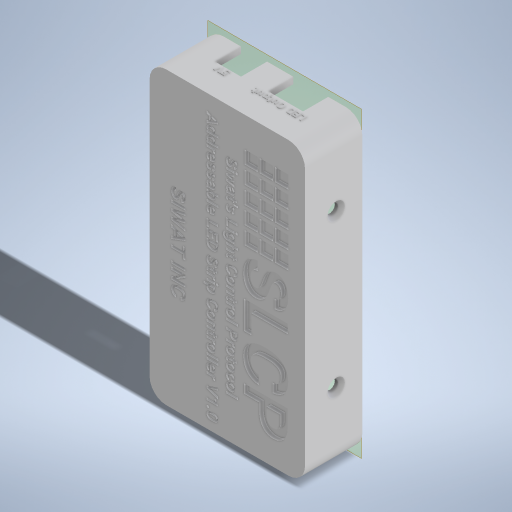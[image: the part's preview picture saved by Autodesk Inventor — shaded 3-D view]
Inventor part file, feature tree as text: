
AUTODESK INVENTOR PART (.ipt)
format: ipt  version: 2023 (Build 270158000, 158)  size: 2,656,768 bytes
history: native  units: in
note: dims shown in document units (in); Inventor stores cm internally (conversion verified against a paired STEP export)
features: reference x28, extrude x13, sketch x12, projected_geometry x4, other x3, plane x2, chamfer x1
ambient origin geometry x8: Origin, YZ Plane, XZ Plane, XY Plane, X Axis, Y Axis, Z Axis, Center Point
bodies: Solid1 (feature_tree)
feature tree (63):
  plane  "Work Plane1"
  extrude  "Extrusion1"  Depth=0.0591in
  extrude  "Extrusion2"  Depth=2.0438in TaperAngle=0.0deg
  extrude  "Extrusion3"  Depth=0.0079in
  extrude  "Extrusion4"  Depth=0.0079in TaperAngle=0.0deg
  sketch  "Sketch5"  dims[d13=0.0984in d14=0.0in d15=0.1644in d16=0.0in]
  plane  "Work Plane2"
  extrude  "Extrusion5"  Depth=0.1644in TaperAngle=0.0deg
  extrude  "Extrusion6"  Depth=0.248in TaperAngle=0.0deg
  extrude  "Extrusion7"  Depth=0.0118in
  extrude  "Extrusion8"  Depth=0.0118in
  chamfer  "Chamfer2"  Distance=0.248in
  extrude  "Extrusion9"  Depth=0.0079in
  extrude  "Extrusion10"  Depth=0.0177in TaperAngle=0.0deg
  extrude  "Extrusion11"  Depth=0.1181in
  extrude  "Extrusion12"  Depth=0.0079in
  extrude  "Extrusion13"  Depth=0.0079in TaperAngle=0.0deg
  sketch  "Sketch1"  dims[d0=0.0118in d1=0.0591in]
  reference  "Reference1"
  sketch  "Sketch2"  dims[d2=0.4188in d3=0.0in d4=2.0438in d5=2.0438in d6=0.0in d7=0.0in]
  reference  "Reference2"
  reference  "Reference3"
  sketch  "Sketch3"  dims[d8=0.0236in d9=0.0079in]
  reference  "Reference4"
  sketch  "Sketch4"  dims[d10=0.0079in d11=2.0438in d12=0.0in]
  reference  "Reference5"
  reference  "Reference6"
  reference  "Reference7"
  reference  "Reference8"
  reference  "Reference9"
  reference  "Reference10"
  reference  "Reference11"
  reference  "Reference12"
  reference  "Reference13"
  reference  "Reference14"
  reference  "Reference15"
  reference  "Reference16"
  reference  "Reference17"
  reference  "Reference18"
  reference  "Reference19"
  reference  "Reference20"
  reference  "Reference21"
  reference  "Reference22"
  reference  "Reference23"
  reference  "Reference24"
  reference  "Reference25"
  reference  "Reference26"
  reference  "Reference27"
  reference  "Reference28"
  sketch  "Sketch7"  dims[d17=0.1969in d18=0.0in d19=0.248in d20=0.0in]
  sketch  "Sketch8"  dims[d21=0.0118in d22=0.0118in]
  projected_geometry  "Projected Loop1"
  sketch  "Sketch9"  dims[d23=0.0118in d24=0.0118in d25=0.248in d26=0.0in]
  projected_geometry  "Projected Loop2"
  projected_geometry  "Projected Loop3"
  projected_geometry  "Projected Loop4"
  sketch  "Sketch10"  dims[d30=0.0079in d31=0.0079in]
  sketch  "Sketch11"  dims[d32=0.0315in d33=0.0787in d34=60.0deg d35=0.0177in d36=0.0in]
  sketch  "Sketch12"  dims[d37=0.1181in d38=0.1181in]
  sketch  "Sketch13"  dims[d39=0.0394in d40=1.9685in d42=0.1575in d43=1.1811in d45=0.1378in d48=0.0394in d49=0.0in d50=0.0079in d51=0.0in d52=0.0079in d53=0.0in d54=0.0079in d55=0.0in]
  parser-record x1  (decoder bookkeeping rows leaked as tree rows — omitted from the tree; the rows remain in map.json)
  other  "Casing.iam"
  other  "Base:1"
note: 1 file-system path scrubbed to <path> (originals preserved in map.json)
